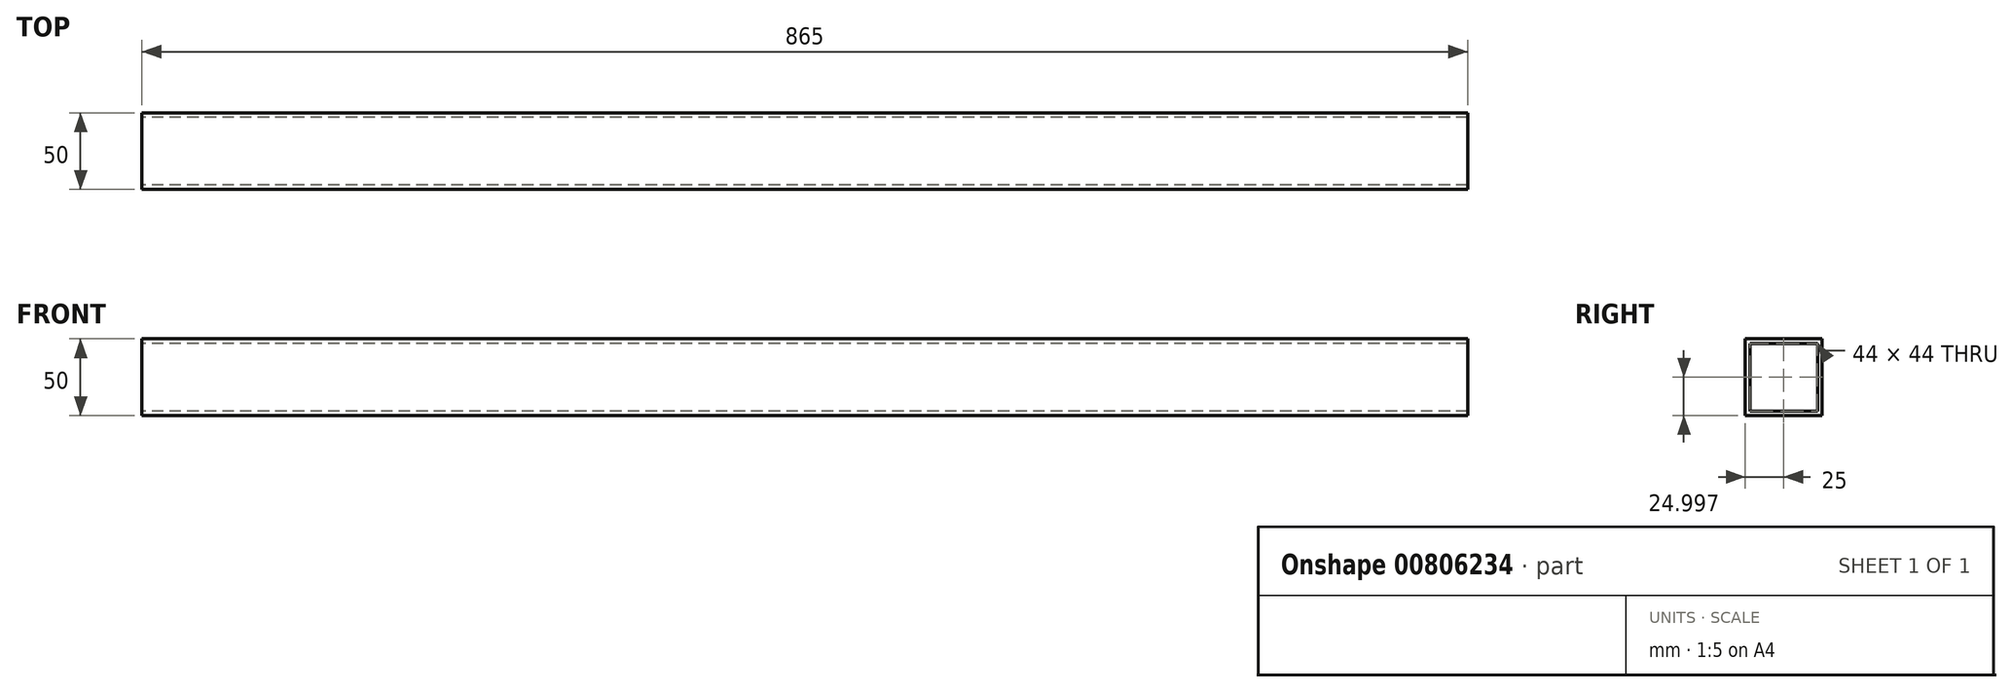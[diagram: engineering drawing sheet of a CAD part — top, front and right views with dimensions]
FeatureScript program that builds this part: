
annotation { "Feature Type Name" : "Feature", "Feature Type Description" : "" }
export const myFeature = defineFeature(function(context is Context, id is Id, definition is map)
    precondition{}
    {
        {
            var Q0;
            Q0=qCreatedBy(makeId("Right.planeOp"),FACE);
            var sketch = newSketch(context, id + "F0", { "sketchPlane" : qUnion([Q0])});
            skLineSegment(sketch, "E0.bottom", {"start": v(-45.22, -30.72) * mm, "end": v(-95.22, -30.72) * mm});
            skLineSegment(sketch, "E0.top", {"start": v(-45.22, 19.28) * mm, "end": v(-95.22, 19.28) * mm});
            skLineSegment(sketch, "E0.left", {"start": v(-45.22, -30.72) * mm, "end": v(-45.22, 19.28) * mm});
            skLineSegment(sketch, "E0.right", {"start": v(-95.22, -30.72) * mm, "end": v(-95.22, 19.28) * mm});
            skPoint(sketch, "E0.middle", {"position": v(-70.22, -5.72) * mm});
            skLineSegment(sketch, "E1.0", {"start": v(-92.22, -27.72) * mm, "end": v(-92.22, 16.28) * mm});
            skLineSegment(sketch, "E1.1", {"start": v(-48.22, -27.72) * mm, "end": v(-92.22, -27.72) * mm});
            skLineSegment(sketch, "E1.2", {"start": v(-48.22, -27.72) * mm, "end": v(-48.22, 16.28) * mm});
            skLineSegment(sketch, "E1.3", {"start": v(-48.22, 16.28) * mm, "end": v(-92.22, 16.28) * mm});
            skSolve(sketch);
        }
        {
            var Q0;
            Q0=qSketchRegion(id+"F0",true);
            extrude(context, id + "F1", {"entities" : qUnion([Q0]), "depth" : 865 * mm, "offsetDistance" : 25 * mm});
        }
    });
